# Revit family: 01-Acabamento para valvula de descarga antivandalismo - Salvagua - DocolSystem
name_source: partatom
category: Conexões hidráulicas
revit_build: Autodesk Revit MEP 2014 (Build: 20131024_2115(x64)
units: mm (PartAtom-declared; Revit-internal decimal feet)

## types (1)
- 1 1/2" e 1 1/4"
    Conexão CW = Sim
    Conexão HW = Sim
    Conexão de resíduos = Sim
    Conexão de ventilação = Sim
    Descrição = Acabamento para válvula de descarga antivandalismo, Salvágua - DocolSystem
    Docol: Acabamento = Cromado
    Docol: Ambiente = Banheiro
    Docol: Bitola = 1 1/2" e 1 1/4"
    Docol: Categoria = Acabamentos para Válvula de Descarga
    Docol: Código = 00572706
    Docol: Descrição = Acabamento para válvula de descarga antivandalismo, Salvágua - DocolSystem
    Docol: Fabricante = Docol
    Docol: Linha = Salvágua
    Docol: Link do Produto = http://www.docol.com.br
    Elevação-padrão = 900  [stored 2.95276 ft]
    Fabricante = Docol
    Modelo = 00572706
    URL = www.docol.com.br

note: [stored X ft] marks values corroborated as IEEE doubles in the binary element streams (Revit-internal decimal feet)

## geometry (parser evidence)
native form markers: Sweep x1
no freeform markers — native parametric forms only
